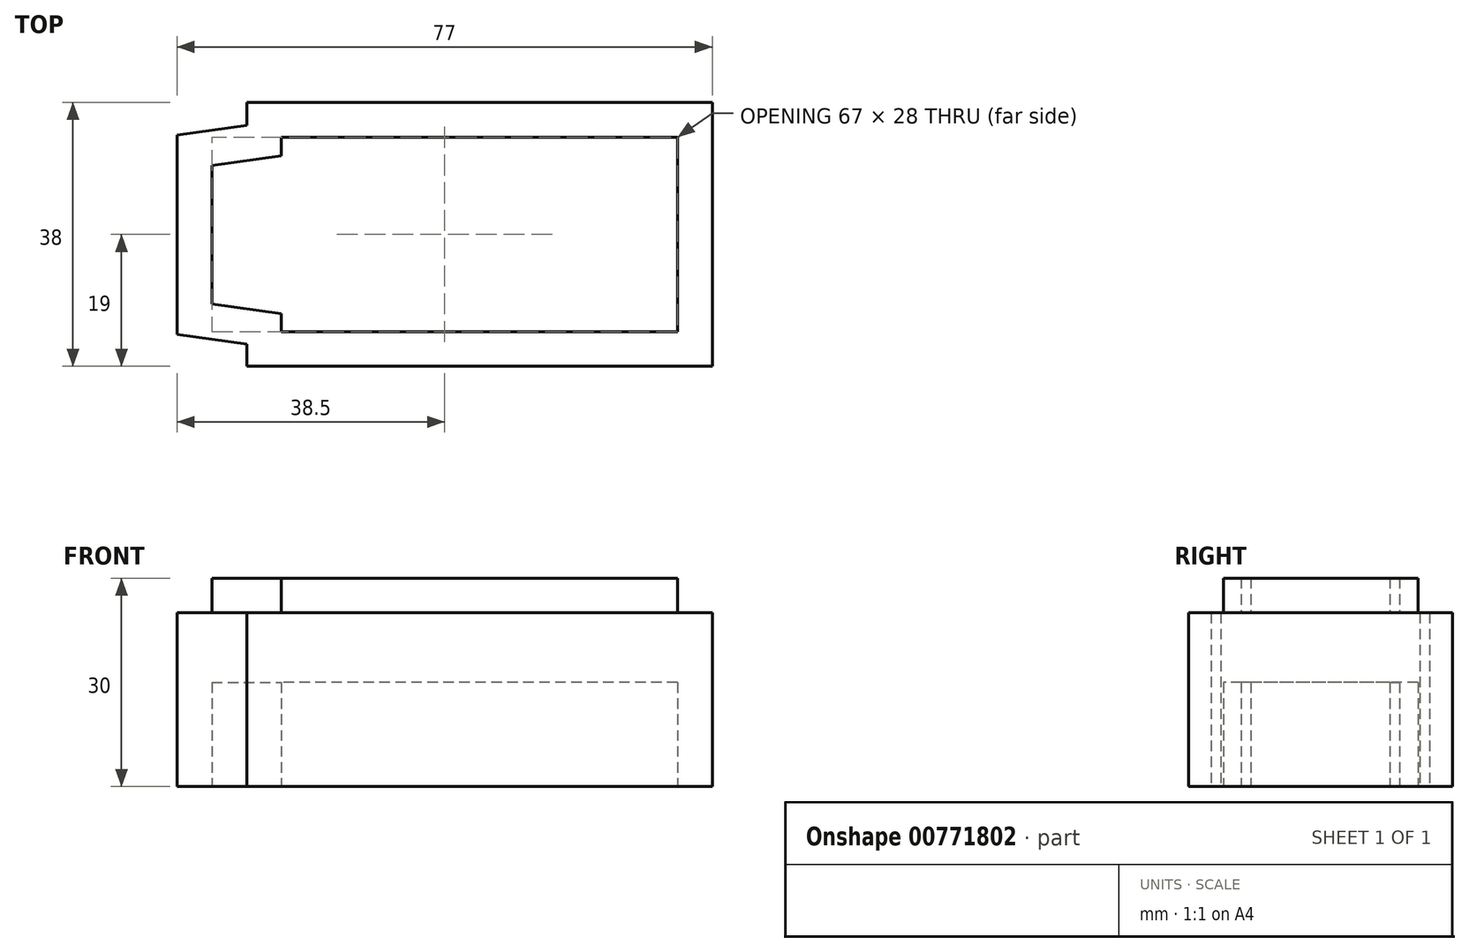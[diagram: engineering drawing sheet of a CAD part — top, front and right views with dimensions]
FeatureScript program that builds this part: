
annotation { "Feature Type Name" : "Feature", "Feature Type Description" : "" }
export const myFeature = defineFeature(function(context is Context, id is Id, definition is map)
    precondition{}
    {
        {
            var Q0;
            Q0=qCreatedBy(makeId("Top.planeOp"),FACE);
            var sketch = newSketch(context, id + "F0", { "sketchPlane" : qUnion([Q0])});
            skLineSegment(sketch, "E0.bottom", {"start": v(28.5, 14) * mm, "end": v(-28.5, 14) * mm});
            skLineSegment(sketch, "E0.top", {"start": v(28.5, -14) * mm, "end": v(-28.5, -14) * mm});
            skLineSegment(sketch, "E0.left", {"start": v(28.5, 14) * mm, "end": v(28.5, -14) * mm});
            skLineSegment(sketch, "E0.right", {"start": v(-28.5, 14) * mm, "end": v(-28.5, -14) * mm});
            skPoint(sketch, "E0.middle", {"position": v(0, 0) * mm});
            skLineSegment(sketch, "E1", {"start": v(-38.5, 9.94) * mm, "end": v(-38.5, -10.04) * mm});
            skLineSegment(sketch, "E2", {"start": v(-38.5, 9.94) * mm, "end": v(-28.5, 11.34) * mm});
            skLineSegment(sketch, "E3", {"start": v(-38.5, -10.04) * mm, "end": v(-28.5, -11.44) * mm});
            skLineSegment(sketch, "E4.0", {"start": v(-33.5, 19) * mm, "end": v(-33.5, -19) * mm});
            skLineSegment(sketch, "E4.1", {"start": v(33.5, 19) * mm, "end": v(-33.5, 19) * mm});
            skLineSegment(sketch, "E4.2", {"start": v(33.5, 19) * mm, "end": v(33.5, -19) * mm});
            skLineSegment(sketch, "E4.3", {"start": v(33.5, -19) * mm, "end": v(-33.5, -19) * mm});
            skLineSegment(sketch, "E5.0", {"start": v(-43.5, -14.4) * mm, "end": v(-29.2, -16.4) * mm});
            skLineSegment(sketch, "E5.1", {"start": v(-43.5, 14.3) * mm, "end": v(-43.5, -14.4) * mm});
            skLineSegment(sketch, "E5.2", {"start": v(-43.5, 14.3) * mm, "end": v(-29.2, 16.3) * mm});
            skSolve(sketch);
        }
        {
            var Q0;
            {var subQ1=sQuery(id+"F0.wireOp",EDGE,"E0.bottom");Q0=makeQuery(id+"F0.imprint","IMPRINT",FACE,{"disambiguationData":[TD([[makeQuery(id+"F0.imprint","IMPRINT",EDGE,{"derivedFrom":subQ1}),1.0]])]});}
            var Q1;
            {var subQ0=sQuery(id+"F0.wireOp",EDGE,"E2");var subQ1=sQuery(id+"F0.wireOp",EDGE,"E0.right");var subQ2=makeQuery(id+"F0.imprint","INTERSECT",VERTEX,{"derivedFrom":[subQ1,subQ0]});Q1=makeQuery(id+"F0.imprint","IMPRINT",FACE,{"disambiguationData":[TD([[makeQuery(id+"F0.imprint","IMPRINT",EDGE,{"disambiguationData":[TD([[subQ2,-1.0]])],"derivedFrom":subQ1}),-1.0]])]});}
            var Q2;
            {var subQ0=sQuery(id+"F0.wireOp",EDGE,"E1");Q2=makeQuery(id+"F0.imprint","IMPRINT",FACE,{"disambiguationData":[TD([[makeQuery(id+"F0.imprint","IMPRINT",EDGE,{"derivedFrom":subQ0}),1.0]])]});}
            extrude(context, id + "F1", {"entities" : qUnion([Q0, Q1, Q2]), "depth" : 30 * mm, "offsetDistance" : 25 * mm, "hasSecondDirection" : true, "secondDirectionOppositeDirection" : false, "secondDirectionDepth" : 15 * mm});
        }
        {
            var Q0;
            {var subQ1=sQuery(id+"F0.wireOp",EDGE,"E1");Q0=makeQuery(id+"F0.imprint","IMPRINT",FACE,{"disambiguationData":[TD([[makeQuery(id+"F0.imprint","IMPRINT",EDGE,{"derivedFrom":subQ1}),-1.0]])]});}
            var Q1;
            {var subQ11=sQuery(id+"F0.wireOp",EDGE,"E0.bottom");Q1=makeQuery(id+"F0.imprint","IMPRINT",FACE,{"disambiguationData":[TD([[makeQuery(id+"F0.imprint","IMPRINT",EDGE,{"derivedFrom":subQ11}),-1.0]])]});}
            extrude(context, id + "F2", {"entities" : qUnion([Q0, Q1]), "operationType" : NewBodyOperationType.ADD, "depth" : 25 * mm, "offsetDistance" : 25 * mm});
        }
    });
